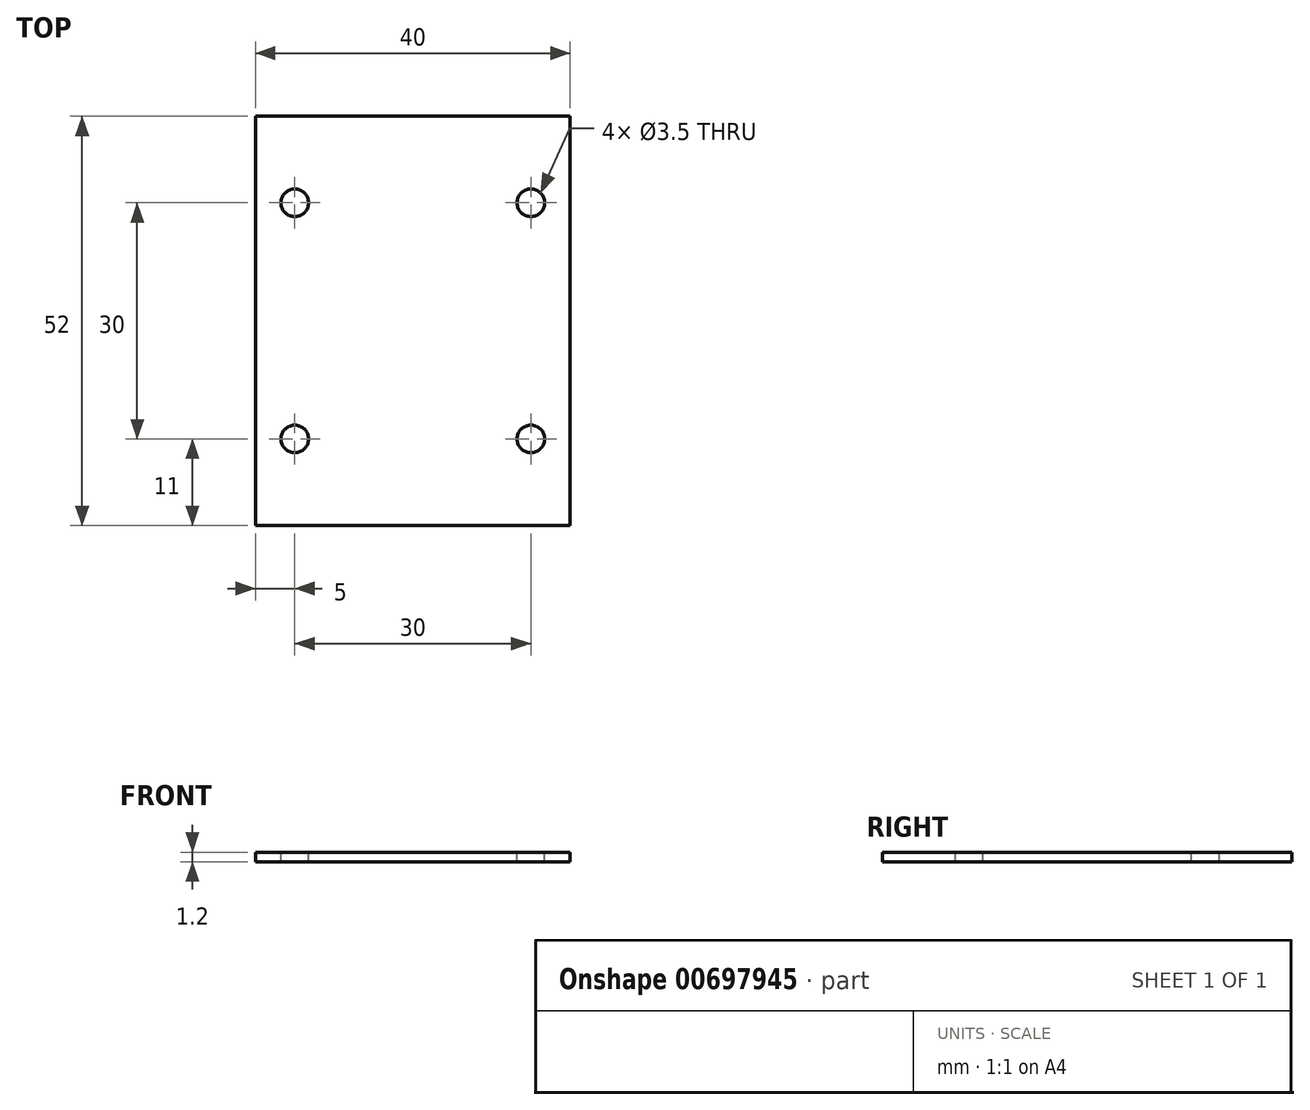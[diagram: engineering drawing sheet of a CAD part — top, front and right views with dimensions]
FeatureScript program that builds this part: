
annotation { "Feature Type Name" : "Feature", "Feature Type Description" : "" }
export const myFeature = defineFeature(function(context is Context, id is Id, definition is map)
    precondition{}
    {
        {
            var Q0;
            Q0=qCreatedBy(makeId("Top.planeOp"),FACE);
            var sketch = newSketch(context, id + "F0", { "sketchPlane" : qUnion([Q0])});
            skLineSegment(sketch, "E0.bottom", {"start": v(20, -26) * mm, "end": v(-20, -26) * mm});
            skLineSegment(sketch, "E0.top", {"start": v(20, 26) * mm, "end": v(-20, 26) * mm});
            skLineSegment(sketch, "E0.left", {"start": v(20, -26) * mm, "end": v(20, 26) * mm});
            skLineSegment(sketch, "E0.right", {"start": v(-20, -26) * mm, "end": v(-20, 26) * mm});
            skPoint(sketch, "E0.middle", {"position": v(0, 0) * mm});
            skSolve(sketch);
        }
        {
            var Q0;
            Q0=makeQuery(id+"F0.imprint","IMPRINT",FACE,{"disambiguationData":[TD([[makeQuery(id+"F0.imprint","IMPRINT",EDGE,{"derivedFrom":sQuery(id+"F0.wireOp",EDGE,"E0.bottom")}),-1.0]])]});
            extrude(context, id + "F1", {"entities" : qUnion([Q0]), "endBound" : BoundingType.SYMMETRIC, "depth" : 1.2 * mm, "offsetDistance" : 25 * mm});
        }
        {
            var Q0;
            Q0=makeQuery(id+"F1.opExtrude","CAP_FACE",FACE,{"disambiguationData":[OSD([sQuery(id+"F0.wireOp",EDGE,"E0.bottom"),sQuery(id+"F0.wireOp",EDGE,"E0.top"),sQuery(id+"F0.wireOp",EDGE,"E0.left"),sQuery(id+"F0.wireOp",EDGE,"E0.right")])],"isStart":false});
            var sketch = newSketch(context, id + "F2", { "sketchPlane" : qUnion([Q0])});
            skLineSegment(sketch, "E1.bottom", {"start": v(15, -15) * mm, "end": v(-15, -15) * mm, "construction": true});
            skLineSegment(sketch, "E1.top", {"start": v(15, 15) * mm, "end": v(-15, 15) * mm, "construction": true});
            skLineSegment(sketch, "E1.left", {"start": v(15, -15) * mm, "end": v(15, 15) * mm, "construction": true});
            skLineSegment(sketch, "E1.right", {"start": v(-15, -15) * mm, "end": v(-15, 15) * mm, "construction": true});
            skPoint(sketch, "E1.middle", {"position": v(0, 0) * mm});
            skCircle(sketch, "E2", {"center": v(-15, 15) * mm, "radius": 1.75 * mm});
            skCircle(sketch, "E3", {"center": v(15, 15) * mm, "radius": 1.75 * mm});
            skCircle(sketch, "E4", {"center": v(-15, -15) * mm, "radius": 1.75 * mm});
            skCircle(sketch, "E5", {"center": v(15, -15) * mm, "radius": 1.75 * mm});
            skSolve(sketch);
        }
        {
            var Q0;
            Q0=qSketchRegion(id+"F2",true);
            extrude(context, id + "F3", {"entities" : qUnion([Q0]), "operationType" : NewBodyOperationType.REMOVE, "endBound" : BoundingType.UP_TO_NEXT, "oppositeDirection" : true, "depth" : 25 * mm, "offsetDistance" : 25 * mm});
        }
    });
